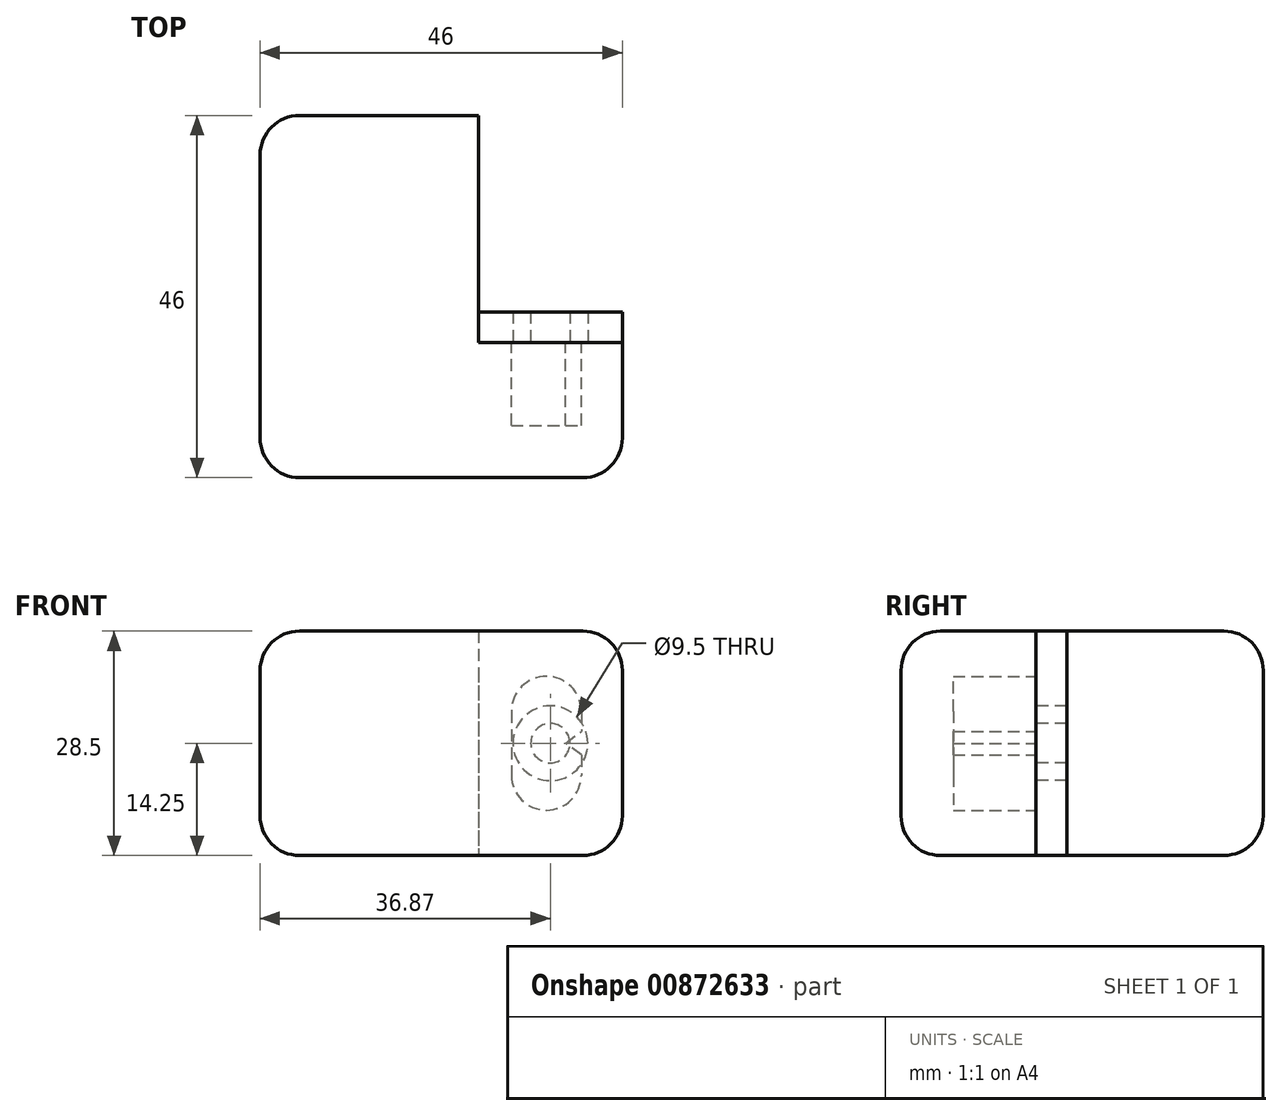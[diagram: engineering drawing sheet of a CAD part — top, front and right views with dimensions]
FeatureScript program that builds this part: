
annotation { "Feature Type Name" : "Feature", "Feature Type Description" : "" }
export const myFeature = defineFeature(function(context is Context, id is Id, definition is map)
    precondition{}
    {
        {
            var Q0;
            Q0=qCreatedBy(makeId("Top.planeOp"),FACE);
            var sketch = newSketch(context, id + "F0", { "sketchPlane" : qUnion([Q0])});
            skLineSegment(sketch, "E0.bottom", {"start": v(23, -23) * mm, "end": v(-23, -23) * mm});
            skLineSegment(sketch, "E0.top", {"start": v(4.74, 23) * mm, "end": v(-23, 23) * mm});
            skLineSegment(sketch, "E0.left", {"start": v(23, -23) * mm, "end": v(23, -5.86) * mm});
            skLineSegment(sketch, "E0.right", {"start": v(-23, -23) * mm, "end": v(-23, 23) * mm});
            skPoint(sketch, "E0.middle", {"position": v(0, 0) * mm});
            skLineSegment(sketch, "E1.0", {"start": v(4.74, -5.86) * mm, "end": v(4.74, 23) * mm});
            skLineSegment(sketch, "E2.0", {"start": v(23, -5.86) * mm, "end": v(4.74, -5.86) * mm});
            skPoint(sketch, "E3.orphan", {"position": v(23, 23) * mm});
            skSolve(sketch);
        }
        {
            var Q0;
            Q0=makeQuery(id+"F0.imprint","IMPRINT",FACE,{"disambiguationData":[TD([[makeQuery(id+"F0.imprint","IMPRINT",EDGE,{"derivedFrom":sQuery(id+"F0.wireOp",EDGE,"E0.bottom")}),-1.0]])]});
            extrude(context, id + "F1", {"entities" : qUnion([Q0]), "endBound" : BoundingType.SYMMETRIC, "depth" : 28.5 * mm, "offsetDistance" : 25 * mm});
        }
        {
            var Q0;
            Q0=makeQuery(id+"F1.opExtrude","CAP_EDGE",EDGE,{"disambiguationData":[OSD([sQuery(id+"F0.wireOp",EDGE,"E0.left")])],"isStart":false});
            var Q1;
            Q1=makeQuery(id+"F1.opExtrude","CAP_EDGE",EDGE,{"disambiguationData":[OSD([sQuery(id+"F0.wireOp",EDGE,"E0.left")])],"isStart":true});
            var Q2;
            Q2=makeQuery(id+"F1.opExtrude","CAP_EDGE",EDGE,{"disambiguationData":[OSD([sQuery(id+"F0.wireOp",EDGE,"E0.top")])],"isStart":false});
            var Q3;
            Q3=makeQuery(id+"F1.opExtrude","CAP_EDGE",EDGE,{"disambiguationData":[OSD([sQuery(id+"F0.wireOp",EDGE,"E0.right")])],"isStart":false});
            var Q4;
            Q4=makeQuery(id+"F1.opExtrude","SWEPT_EDGE",EDGE,{"disambiguationData":[OSD([sQuery(id+"F0.wireOp",EDGE,"E0.top"),sQuery(id+"F0.wireOp",EDGE,"E0.right")])]});
            var Q5;
            Q5=makeQuery(id+"F1.opExtrude","CAP_EDGE",EDGE,{"disambiguationData":[OSD([sQuery(id+"F0.wireOp",EDGE,"E0.top")])],"isStart":true});
            var Q6;
            Q6=makeQuery(id+"F1.opExtrude","CAP_EDGE",EDGE,{"disambiguationData":[OSD([sQuery(id+"F0.wireOp",EDGE,"E0.right")])],"isStart":true});
            var Q7;
            Q7=makeQuery(id+"F1.opExtrude","CAP_EDGE",EDGE,{"disambiguationData":[OSD([sQuery(id+"F0.wireOp",EDGE,"E0.bottom")])],"isStart":true});
            var Q8;
            Q8=makeQuery(id+"F1.opExtrude","CAP_EDGE",EDGE,{"disambiguationData":[OSD([sQuery(id+"F0.wireOp",EDGE,"E0.bottom")])],"isStart":false});
            var Q9;
            Q9=makeQuery(id+"F1.opExtrude","SWEPT_EDGE",EDGE,{"disambiguationData":[OSD([sQuery(id+"F0.wireOp",EDGE,"E0.bottom"),sQuery(id+"F0.wireOp",EDGE,"E0.right")])]});
            var Q10;
            Q10=makeQuery(id+"F1.opExtrude","SWEPT_EDGE",EDGE,{"disambiguationData":[OSD([sQuery(id+"F0.wireOp",EDGE,"E0.bottom"),sQuery(id+"F0.wireOp",EDGE,"E0.left")])]});
            fillet(context, id + "F2", {"entities" : qUnion([Q0, Q1, Q2, Q3, Q4, Q5, Q6, Q7, Q8, Q9, Q10]), "radius" : 5 * mm, "tangentPropagation" : true, "allowEdgeOverflow" : false});
        }
        {
            var Q0;
            Q0=makeQuery(id+"F1.opExtrude","SWEPT_FACE",FACE,{"disambiguationData":[OSD([sQuery(id+"F0.wireOp",EDGE,"E2.0")])]});
            var sketch = newSketch(context, id + "F3", { "sketchPlane" : qUnion([Q0])});
            skLineSegment(sketch, "E4", {"start": v(-23, 0) * mm, "end": v(-4.74, 0) * mm});
            skCircle(sketch, "E5", {"center": v(-13.87, 0) * mm, "radius": 2.5 * mm});
            skCircle(sketch, "E6", {"center": v(-13.87, 0) * mm, "radius": 4.75 * mm});
            skSolve(sketch);
        }
        {
            var Q0;
            {var subQ0=sQuery(id+"F3.wireOp",EDGE,"E6");var subQ1=sQuery(id+"F3.wireOp",EDGE,"E4");var subQ2=makeQuery(id+"F3.imprint","INTERSECT",VERTEX,{"disambiguationData":[OD(0.0)],"derivedFrom":[subQ1,subQ0]});Q0=makeQuery(id+"F3.imprint","IMPRINT",FACE,{"disambiguationData":[TD([[makeQuery(id+"F3.imprint","IMPRINT",EDGE,{"disambiguationData":[TD([[subQ2,-1.0]])],"derivedFrom":subQ1}),1.0]])]});}
            var Q1;
            {var subQ0=sQuery(id+"F3.wireOp",EDGE,"E5");var subQ1=sQuery(id+"F3.wireOp",EDGE,"E4");var subQ2=makeQuery(id+"F3.imprint","INTERSECT",VERTEX,{"disambiguationData":[OD(0.0)],"derivedFrom":[subQ1,subQ0]});Q1=makeQuery(id+"F3.imprint","IMPRINT",FACE,{"disambiguationData":[TD([[makeQuery(id+"F3.imprint","IMPRINT",EDGE,{"disambiguationData":[TD([[subQ2,-1.0]])],"derivedFrom":subQ1}),1.0]])]});}
            var Q2;
            {var subQ0=sQuery(id+"F3.wireOp",EDGE,"E5");var subQ1=sQuery(id+"F3.wireOp",EDGE,"E4");var subQ2=makeQuery(id+"F3.imprint","INTERSECT",VERTEX,{"disambiguationData":[OD(0.0)],"derivedFrom":[subQ1,subQ0]});Q2=makeQuery(id+"F3.imprint","IMPRINT",FACE,{"disambiguationData":[TD([[makeQuery(id+"F3.imprint","IMPRINT",EDGE,{"disambiguationData":[TD([[subQ2,-1.0]])],"derivedFrom":subQ1}),-1.0]])]});}
            var Q3;
            {var subQ0=sQuery(id+"F3.wireOp",EDGE,"E6");var subQ1=sQuery(id+"F3.wireOp",EDGE,"E4");var subQ2=makeQuery(id+"F3.imprint","INTERSECT",VERTEX,{"disambiguationData":[OD(0.0)],"derivedFrom":[subQ1,subQ0]});Q3=makeQuery(id+"F3.imprint","IMPRINT",FACE,{"disambiguationData":[TD([[makeQuery(id+"F3.imprint","IMPRINT",EDGE,{"disambiguationData":[TD([[subQ2,-1.0]])],"derivedFrom":subQ1}),-1.0]])]});}
            extrude(context, id + "F4", {"entities" : qUnion([Q0, Q1, Q2, Q3]), "depth" : 3.9 * mm, "offsetDistance" : 25 * mm});
        }
        {
            var Q0;
            Q0 = qSketchRegion(id + "F3", true);
            extrude(context, id + "F5", {"entities" : qUnion([Q0]), "operationType" : NewBodyOperationType.REMOVE, "depth" : 2.3 * mm, "offsetDistance" : 25 * mm});
        }
        {
            var Q0;
            Q0=makeQuery(id+"F1.opExtrude","SWEPT_FACE",FACE,{"disambiguationData":[OSD([sQuery(id+"F0.wireOp",EDGE,"E1.0")])]});
            var sketch = newSketch(context, id + "F6", { "sketchPlane" : qUnion([Q0])});
            skLineSegment(sketch, "E7", {"start": v(23, 0) * mm, "end": v(10.75, 0) * mm});
            skSolve(sketch);
        }
        {
            var Q0;
            {var subQ4=sQuery(id+"F0.wireOp",EDGE,"E2.0");var subQ11=makeQuery(id+"F1.opExtrude","CAP_EDGE",EDGE,{"disambiguationData":[OSD([subQ4])],"isStart":false});Q0=makeQuery(id+"F3.imprint","IMPRINT",FACE,{"disambiguationData":[TD([[makeQuery(id+"F3.imprint","IMPRINT",EDGE,{"derivedFrom":subQ11}),-1.0]])]});}
            var sketch = newSketch(context, id + "F7", { "sketchPlane" : qUnion([Q0])});
            skLineSegment(sketch, "E8.bottom", {"start": v(-13.36, 8.5) * mm, "end": v(-13.36, 8.5) * mm});
            skLineSegment(sketch, "E8.top", {"start": v(-13.36, -8.5) * mm, "end": v(-13.36, -8.5) * mm});
            skLineSegment(sketch, "E8.left", {"start": v(-8.92, 4.06) * mm, "end": v(-8.92, -4.06) * mm});
            skLineSegment(sketch, "E8.right", {"start": v(-17.8, 4.06) * mm, "end": v(-17.8, -4.06) * mm});
            skPoint(sketch, "E8.middle", {"position": v(-13.36, 0) * mm});
            skPoint(sketch, "E9.visualSharp", {"position": v(-8.92, 8.5) * mm});
            skArc(sketch, "E9.filletArc", {"start": v(-8.92, 4.06) * mm, "mid": v(-10.22, 7.2) * mm, "end": v(-13.36, 8.5) * mm});
            skPoint(sketch, "E10.visualSharp", {"position": v(-17.8, 8.5) * mm});
            skArc(sketch, "E10.filletArc", {"start": v(-13.36, 8.5) * mm, "mid": v(-16.5, 7.2) * mm, "end": v(-17.8, 4.06) * mm});
            skPoint(sketch, "E11.visualSharp", {"position": v(-8.92, -8.5) * mm});
            skArc(sketch, "E11.filletArc", {"start": v(-13.36, -8.5) * mm, "mid": v(-10.22, -7.2) * mm, "end": v(-8.92, -4.06) * mm});
            skPoint(sketch, "E12.visualSharp", {"position": v(-17.8, -8.5) * mm});
            skArc(sketch, "E12.filletArc", {"start": v(-17.8, -4.06) * mm, "mid": v(-16.5, -7.2) * mm, "end": v(-13.36, -8.5) * mm});
            skLineSegment(sketch, "E13", {"start": v(-17.8, 0) * mm, "end": v(-15.8, 0) * mm});
            skLineSegment(sketch, "E14", {"start": v(-15.8, 0) * mm, "end": v(-17.8, 1.5) * mm});
            skLineSegment(sketch, "E15", {"start": v(-17.8, 1.5) * mm, "end": v(-15.8, 0) * mm});
            skLineSegment(sketch, "E16", {"start": v(-17.8, -1.5) * mm, "end": v(-15.8, 0) * mm});
            skSolve(sketch);
        }
        {
            var Q0;
            {var subQ0=sQuery(id+"F7.wireOp",EDGE,"E11.filletArc");Q0=makeQuery(id+"F7.imprint","IMPRINT",FACE,{"disambiguationData":[TD([[makeQuery(id+"F7.imprint","IMPRINT",EDGE,{"derivedFrom":subQ0}),1.0]])]});}
            var Q1;
            {var subQ1=sQuery(id+"F7.wireOp",EDGE,"E9.filletArc");Q1=makeQuery(id+"F7.imprint","IMPRINT",FACE,{"disambiguationData":[TD([[makeQuery(id+"F7.imprint","IMPRINT",EDGE,{"derivedFrom":subQ1}),1.0]])]});}
            extrude(context, id + "F8", {"entities" : qUnion([Q0, Q1]), "operationType" : NewBodyOperationType.REMOVE, "oppositeDirection" : true, "depth" : 10.5 * mm, "offsetDistance" : 25 * mm});
        }
    });
